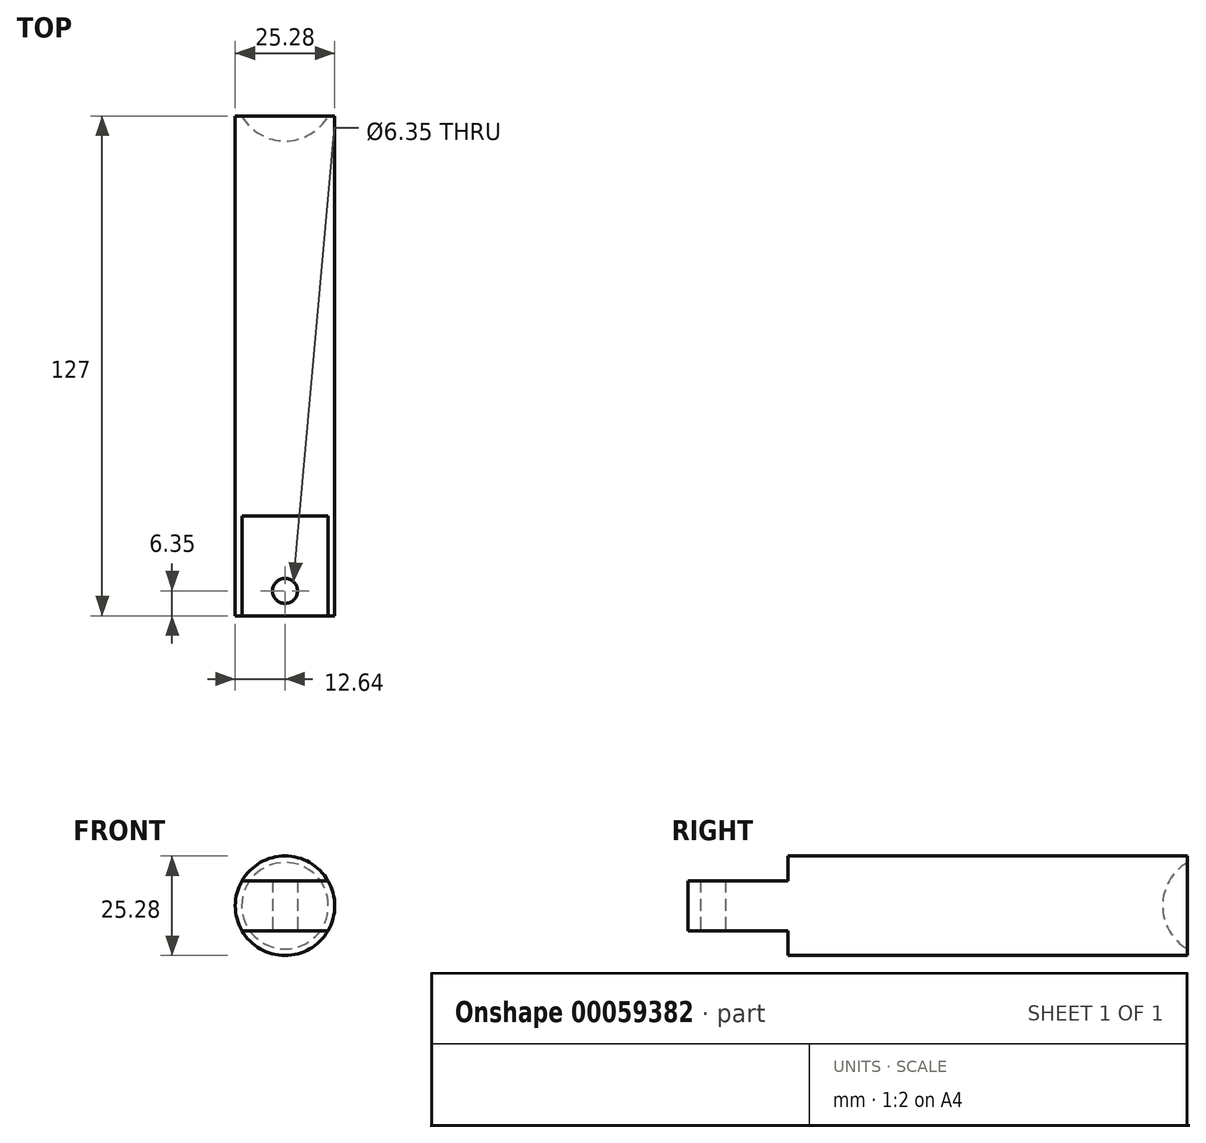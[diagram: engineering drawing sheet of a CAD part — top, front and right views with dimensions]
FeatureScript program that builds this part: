
annotation { "Feature Type Name" : "Feature", "Feature Type Description" : "" }
export const myFeature = defineFeature(function(context is Context, id is Id, definition is map)
    precondition{}
    {
        {
            var Q0;
            Q0=qCreatedBy(makeId("Front.planeOp"),FACE);
            var sketch = newSketch(context, id + "F0", { "sketchPlane" : qUnion([Q0])});
            skCircle(sketch, "E0", {"center": v(0, 0) * mm, "radius": 12.64 * mm});
            skSolve(sketch);
        }
        {
            var Q0;
            Q0 = qSketchRegion(id + "F0", true);
            extrude(context, id + "F1", {"entities" : qUnion([Q0]), "oppositeDirection" : true, "depth" : 127 * mm});
        }
        {
            var Q0;
            Q0=makeQuery(id+"F1.opExtrude","CAP_FACE",FACE,{"disambiguationData":[OSD([sQuery(id+"F0.wireOp",EDGE,"E0")])],"isStart":true});
            var sketch = newSketch(context, id + "F2", { "sketchPlane" : qUnion([Q0])});
            skLineSegment(sketch, "E1.bottom", {"start": v(-19.55, -15.48) * mm, "end": v(21.41, -15.48) * mm});
            skLineSegment(sketch, "E1.top", {"start": v(-19.55, 15.7) * mm, "end": v(21.41, 15.7) * mm});
            skLineSegment(sketch, "E2", {"start": v(-19.55, -15.48) * mm, "end": v(-19.55, -6.35) * mm});
            skLineSegment(sketch, "E3", {"start": v(21.41, -6.35) * mm, "end": v(21.41, -15.48) * mm});
            skLineSegment(sketch, "E4", {"start": v(21.41, -6.35) * mm, "end": v(-19.55, -6.35) * mm});
            skLineSegment(sketch, "E5", {"start": v(-19.55, 15.7) * mm, "end": v(-19.55, 6.35) * mm});
            skLineSegment(sketch, "E6", {"start": v(21.41, 6.35) * mm, "end": v(-19.55, 6.35) * mm});
            skLineSegment(sketch, "E7", {"start": v(21.41, 6.35) * mm, "end": v(21.41, 15.7) * mm});
            skSolve(sketch);
        }
        {
            var Q0;
            Q0 = qSketchRegion(id + "F2", true);
            extrude(context, id + "F3", {"entities" : qUnion([Q0]), "operationType" : NewBodyOperationType.REMOVE, "oppositeDirection" : true, "depth" : 25.4 * mm});
        }
        {
            var Q0;
            Q0=makeQuery(id+"F3.boolean.opBoolean","COPY",FACE,{"derivedFrom":makeQuery(id+"F3.opExtrude","SWEPT_FACE",FACE,{"disambiguationData":[OSD([sQuery(id+"F2.wireOp",EDGE,"E4")])]})});
            var sketch = newSketch(context, id + "F4", { "sketchPlane" : qUnion([Q0])});
            skCircle(sketch, "E8", {"center": v(0, -6.35) * mm, "radius": 3.18 * mm});
            skSolve(sketch);
        }
        {
            var Q0;
            Q0 = qSketchRegion(id + "F4", true);
            extrude(context, id + "F5", {"entities" : qUnion([Q0]), "operationType" : NewBodyOperationType.REMOVE, "endBound" : BoundingType.UP_TO_NEXT, "oppositeDirection" : true, "depth" : 25.4 * mm});
        }
        {
            var Q0;
            Q0=qCreatedBy(makeId("Top.planeOp"),FACE);
            var sketch = newSketch(context, id + "F6", { "sketchPlane" : qUnion([Q0])});
            skArc(sketch, "E9", {"start": v(12.7, 133.35) * mm, "mid": v(0, 146.05) * mm, "end": v(-12.7, 133.35) * mm});
            skLineSegment(sketch, "E10", {"start": v(0, 133.35) * mm, "end": v(-12.7, 133.35) * mm});
            skLineSegment(sketch, "E11", {"start": v(0, 133.35) * mm, "end": v(12.7, 133.35) * mm});
            skSolve(sketch);
        }
        {
            var Q0;
            Q0 = qSketchRegion(id + "F6", true);
            var Q1;
            Q1=sQuery(id+"F6.wireOp",EDGE,"E10");
            revolve(context, id + "F7", {"operationType" : NewBodyOperationType.REMOVE, "entities" : qUnion([Q0]), "axis" : qUnion([Q1]), "revolveType" : RevolveType.FULL, "oppositeDirection" : true});
        }
    });
